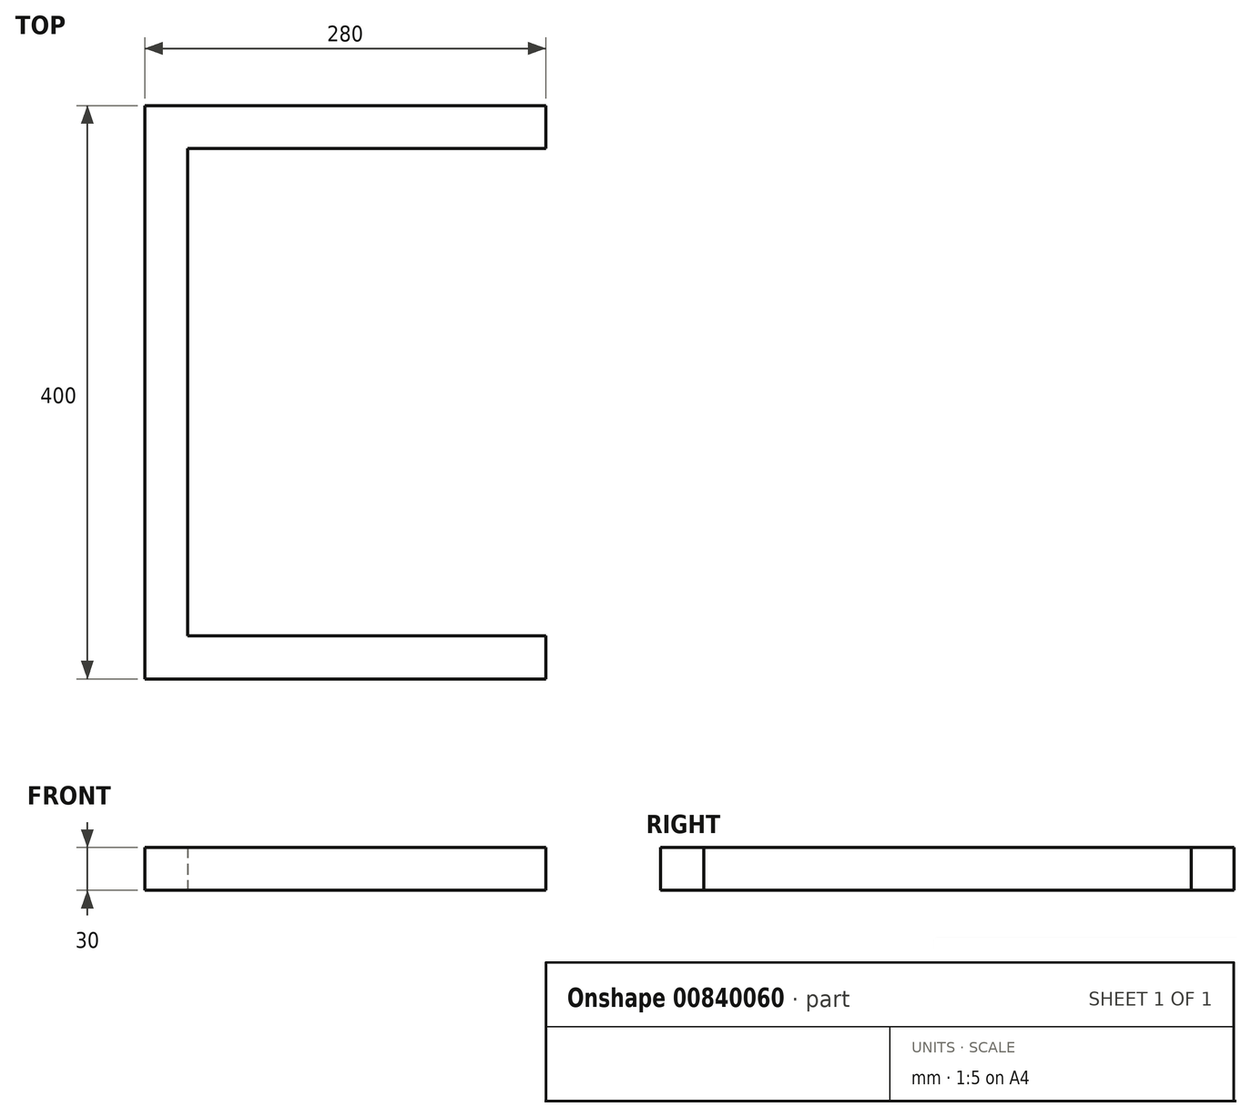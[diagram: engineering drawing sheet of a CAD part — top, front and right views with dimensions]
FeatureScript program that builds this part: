
annotation { "Feature Type Name" : "Feature", "Feature Type Description" : "" }
export const myFeature = defineFeature(function(context is Context, id is Id, definition is map)
    precondition{}
    {
        {
            var Q0;
            Q0=qCreatedBy(makeId("Top.planeOp"),FACE);
            var sketch = newSketch(context, id + "F0", { "sketchPlane" : qUnion([Q0])});
            skLineSegment(sketch, "E0", {"start": v(0, 157.5) * mm, "end": v(-250, 157.5) * mm});
            skLineSegment(sketch, "E1", {"start": v(-250, 157.5) * mm, "end": v(-250, -182.5) * mm});
            skLineSegment(sketch, "E2", {"start": v(-250, -182.5) * mm, "end": v(0, -182.5) * mm});
            skLineSegment(sketch, "E3", {"start": v(0, -182.5) * mm, "end": v(0, -212.5) * mm});
            skLineSegment(sketch, "E4", {"start": v(0, -212.5) * mm, "end": v(-280, -212.5) * mm});
            skLineSegment(sketch, "E5", {"start": v(-280, -212.5) * mm, "end": v(-280, 187.5) * mm});
            skLineSegment(sketch, "E6", {"start": v(-280, 187.5) * mm, "end": v(0, 187.5) * mm});
            skLineSegment(sketch, "E7", {"start": v(0, 187.5) * mm, "end": v(0, 157.5) * mm});
            skSolve(sketch);
        }
        {
            var Q0;
            Q0=makeQuery(id+"F0.imprint","IMPRINT",FACE,{"disambiguationData":[TD([[makeQuery(id+"F0.imprint","IMPRINT",EDGE,{"derivedFrom":sQuery(id+"F0.wireOp",EDGE,"E0")}),-1.0]])]});
            extrude(context, id + "F1", {"entities" : qUnion([Q0]), "endBound" : BoundingType.SYMMETRIC, "depth" : 30 * mm, "offsetDistance" : 25 * mm});
        }
    });
